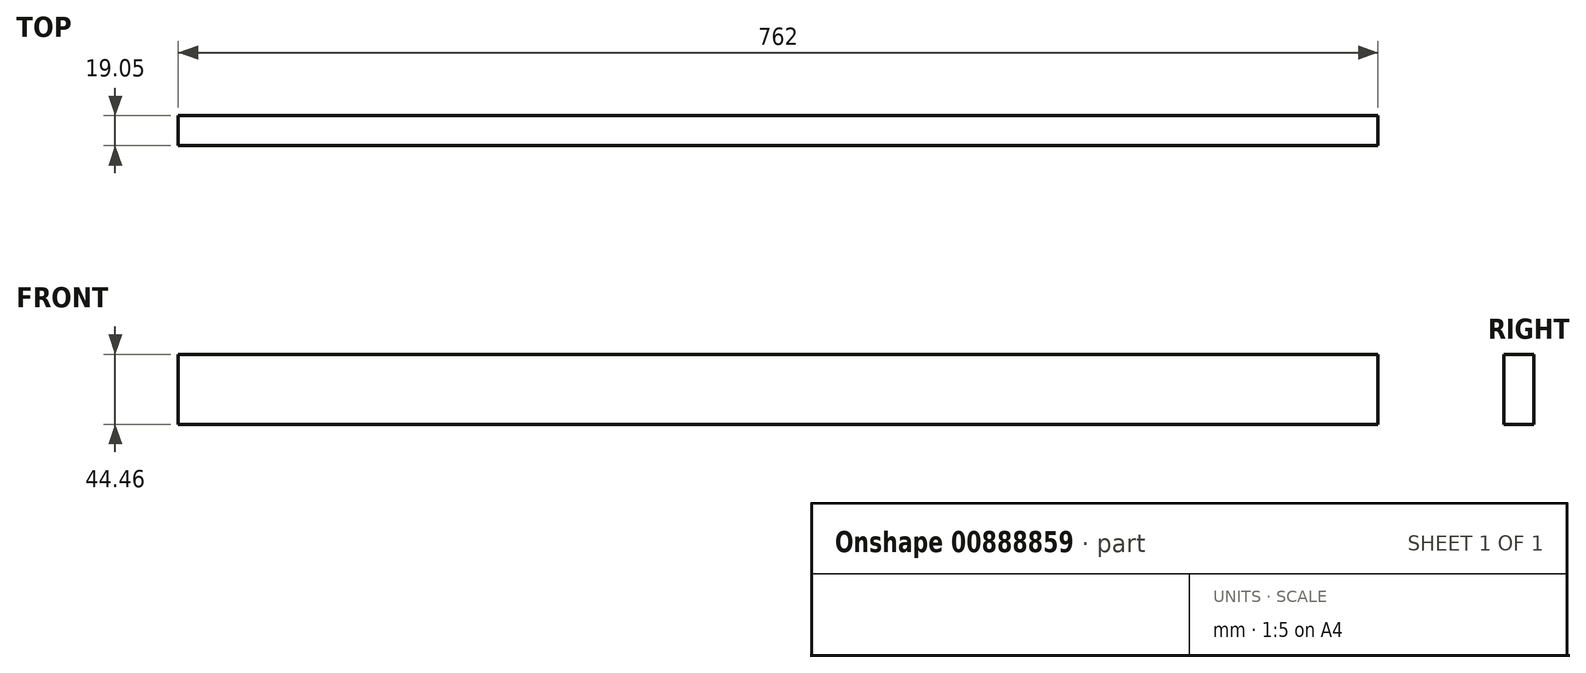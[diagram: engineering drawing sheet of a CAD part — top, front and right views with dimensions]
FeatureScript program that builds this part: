
annotation { "Feature Type Name" : "Feature", "Feature Type Description" : "" }
export const myFeature = defineFeature(function(context is Context, id is Id, definition is map)
    precondition{}
    {
        {
            var Q0;
            Q0=qCreatedBy(makeId("Front.planeOp"),FACE);
            var sketch = newSketch(context, id + "F0", { "sketchPlane" : qUnion([Q0])});
            skLineSegment(sketch, "E0.bottom", {"start": v(381, -22.22) * mm, "end": v(-381, -22.23) * mm});
            skLineSegment(sketch, "E0.top", {"start": v(381, 22.23) * mm, "end": v(-381, 22.23) * mm});
            skLineSegment(sketch, "E0.left", {"start": v(381, -22.22) * mm, "end": v(381, 22.23) * mm});
            skLineSegment(sketch, "E0.right", {"start": v(-381, -22.23) * mm, "end": v(-381, 22.23) * mm});
            skPoint(sketch, "E0.middle", {"position": v(0, 0) * mm});
            skSolve(sketch);
        }
        {
            var Q0;
            Q0=makeQuery(id+"F0.imprint","IMPRINT",FACE,{"disambiguationData":[TD([[makeQuery(id+"F0.imprint","IMPRINT",EDGE,{"derivedFrom":sQuery(id+"F0.wireOp",EDGE,"E0.bottom")}),-1.0]])]});
            extrude(context, id + "F1", {"entities" : qUnion([Q0]), "depth" : 19.05 * mm, "offsetDistance" : 25.4 * mm});
        }
    });
